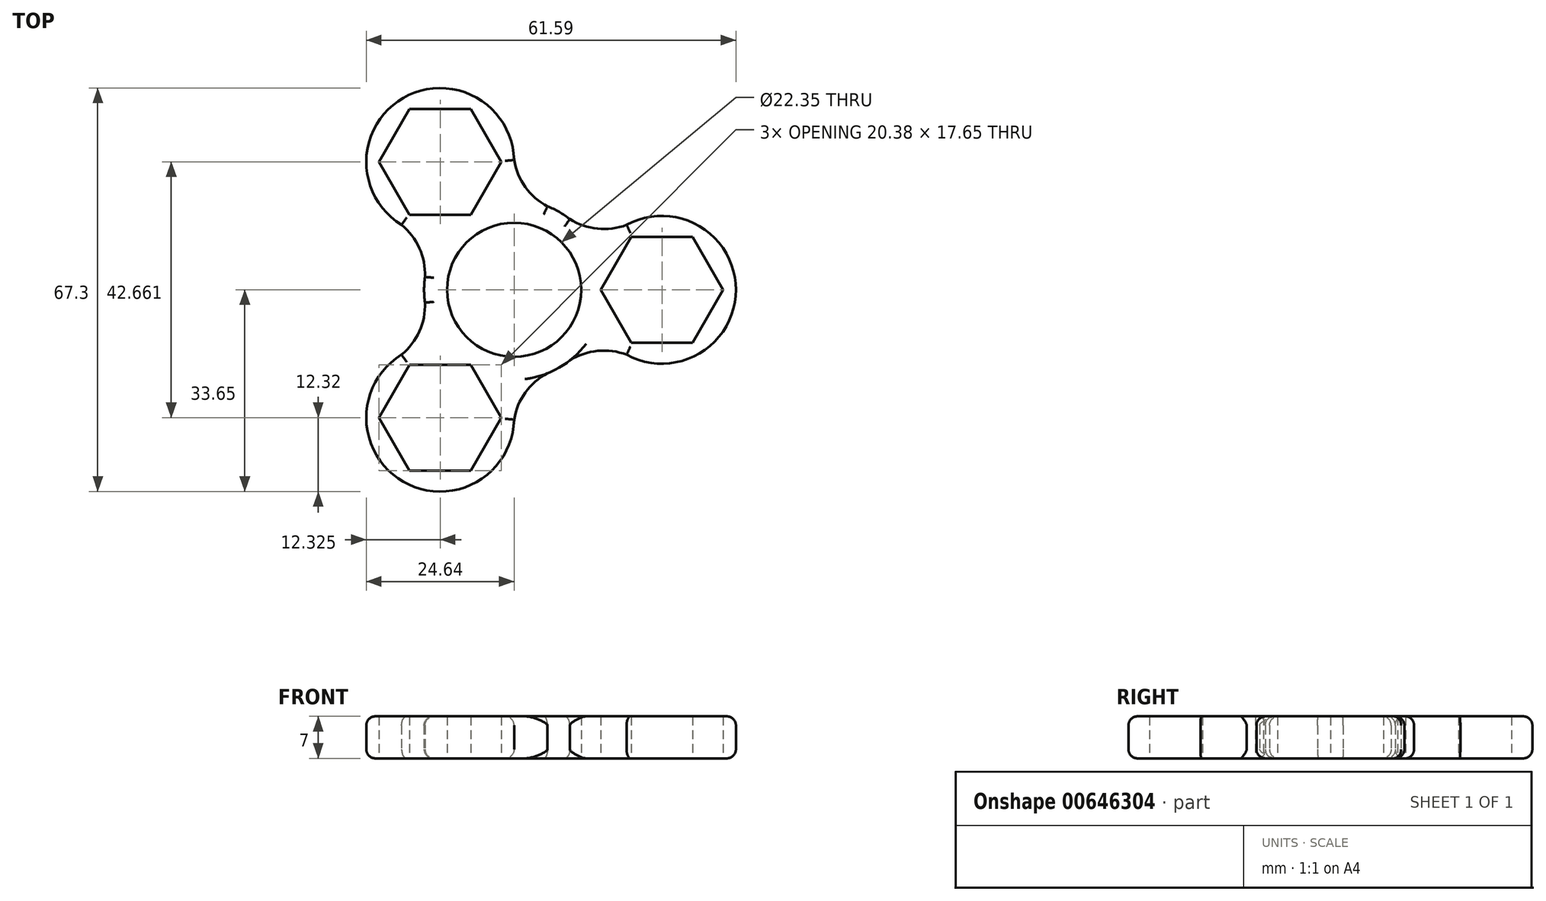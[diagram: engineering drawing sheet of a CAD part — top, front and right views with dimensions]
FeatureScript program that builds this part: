
annotation { "Feature Type Name" : "Feature", "Feature Type Description" : "" }
export const myFeature = defineFeature(function(context is Context, id is Id, definition is map)
    precondition{}
    {
        {
            var Q0;
            Q0=qCreatedBy(makeId("Top.planeOp"),FACE);
            var sketch = newSketch(context, id + "F0", { "sketchPlane" : qUnion([Q0])});
            skCircle(sketch, "E0", {"center": v(0, 0) * mm, "radius": 11.18 * mm});
            skArc(sketch, "E1", {"start": v(9.28, 11.79) * mm, "mid": v(7.5, 13) * mm, "end": v(5.57, 13.93) * mm});
            skLineSegment(sketch, "E2", {"start": v(0, 0) * mm, "end": v(35, 0) * mm, "construction": true});
            skCircle(sketch, "E3.cCircle", {"center": v(24.63, 0) * mm, "radius": 8.82 * mm, "construction": true});
            skLineSegment(sketch, "E3.0", {"start": v(19.54, 8.82) * mm, "end": v(29.73, 8.82) * mm});
            skLineSegment(sketch, "E3.1", {"start": v(29.73, 8.82) * mm, "end": v(34.82, 0) * mm});
            skLineSegment(sketch, "E3.2", {"start": v(34.82, 0) * mm, "end": v(29.73, -8.82) * mm});
            skLineSegment(sketch, "E3.3", {"start": v(29.73, -8.82) * mm, "end": v(19.54, -8.82) * mm});
            skLineSegment(sketch, "E3.4", {"start": v(19.54, -8.82) * mm, "end": v(14.44, 0) * mm});
            skLineSegment(sketch, "E3.5", {"start": v(14.44, 0) * mm, "end": v(19.54, 8.82) * mm});
            skPoint(sketch, "E3.0.midPoint", {"position": v(24.63, 8.82) * mm});
            skArc(sketch, "E4", {"start": v(18.75, -10.83) * mm, "mid": v(36.95, 0) * mm, "end": v(18.75, 10.83) * mm});
            skArc(sketch, "E5", {"start": v(18.75, -10.83) * mm, "mid": v(13.9, -10.2) * mm, "end": v(9.28, -11.79) * mm});
            skArc(sketch, "E6.MirrorCS", {"start": v(18.75, 10.83) * mm, "mid": v(13.9, 10.2) * mm, "end": v(9.28, 11.79) * mm});
            skPoint(sketch, "E7.orphan", {"position": v(13.8, 5.88) * mm});
            skLineSegment(sketch, "E8.1.0", {"start": v(-7.22, 12.5) * mm, "end": v(-17.41, 12.5) * mm});
            skPoint(sketch, "E8.1.1", {"position": v(-19.96, 16.92) * mm});
            skArc(sketch, "E8.1.2", {"start": v(-18.75, 10.82) * mm, "mid": v(-15.78, 6.94) * mm, "end": v(-14.85, 2.14) * mm});
            skArc(sketch, "E8.1.3", {"start": v(0, 21.65) * mm, "mid": v(-18.48, 32) * mm, "end": v(-18.75, 10.82) * mm});
            skLineSegment(sketch, "E8.1.4", {"start": v(0, 0) * mm, "end": v(-17.5, 30.31) * mm, "construction": true});
            skCircle(sketch, "E8.1.5", {"center": v(-12.32, 21.33) * mm, "radius": 8.82 * mm, "construction": true});
            skLineSegment(sketch, "E8.1.6", {"start": v(-17.41, 12.5) * mm, "end": v(-22.5, 21.33) * mm});
            skLineSegment(sketch, "E8.1.7", {"start": v(-22.5, 21.33) * mm, "end": v(-17.41, 30.16) * mm});
            skLineSegment(sketch, "E8.1.8", {"start": v(-17.41, 30.16) * mm, "end": v(-7.22, 30.16) * mm});
            skLineSegment(sketch, "E8.1.9", {"start": v(-7.22, 30.16) * mm, "end": v(-2.12, 21.33) * mm});
            skArc(sketch, "E8.1.10", {"start": v(0, 21.65) * mm, "mid": v(1.88, 17.13) * mm, "end": v(5.57, 13.93) * mm});
            skLineSegment(sketch, "E8.1.11", {"start": v(-2.12, 21.33) * mm, "end": v(-7.22, 12.5) * mm});
            skLineSegment(sketch, "E8.2.0", {"start": v(-7.22, -12.5) * mm, "end": v(-2.12, -21.33) * mm});
            skPoint(sketch, "E8.2.1", {"position": v(-4.67, -25.74) * mm});
            skArc(sketch, "E8.2.2", {"start": v(0, -21.65) * mm, "mid": v(1.88, -17.13) * mm, "end": v(5.57, -13.93) * mm});
            skArc(sketch, "E8.2.3", {"start": v(-18.75, -10.82) * mm, "mid": v(-18.48, -32) * mm, "end": v(0, -21.65) * mm});
            skLineSegment(sketch, "E8.2.4", {"start": v(0, 0) * mm, "end": v(-17.5, -30.31) * mm, "construction": true});
            skCircle(sketch, "E8.2.5", {"center": v(-12.32, -21.33) * mm, "radius": 8.82 * mm, "construction": true});
            skLineSegment(sketch, "E8.2.6", {"start": v(-2.12, -21.33) * mm, "end": v(-7.22, -30.16) * mm});
            skLineSegment(sketch, "E8.2.7", {"start": v(-7.22, -30.16) * mm, "end": v(-17.41, -30.16) * mm});
            skLineSegment(sketch, "E8.2.8", {"start": v(-17.41, -30.16) * mm, "end": v(-22.5, -21.33) * mm});
            skLineSegment(sketch, "E8.2.9", {"start": v(-22.5, -21.33) * mm, "end": v(-17.41, -12.5) * mm});
            skArc(sketch, "E8.2.10", {"start": v(-18.75, -10.82) * mm, "mid": v(-15.78, -6.94) * mm, "end": v(-14.85, -2.14) * mm});
            skLineSegment(sketch, "E8.2.11", {"start": v(-17.41, -12.5) * mm, "end": v(-7.22, -12.5) * mm});
            skPoint(sketch, "E9.trimOffspring.end.orphan", {"position": v(-9.28, 11.79) * mm});
            skArc(sketch, "E10.trimOffspring", {"start": v(-14.85, 2.14) * mm, "mid": v(-15, 0) * mm, "end": v(-14.85, -2.14) * mm});
            skArc(sketch, "E11.trimOffspring", {"start": v(5.57, -13.93) * mm, "mid": v(7.5, -13) * mm, "end": v(9.28, -11.79) * mm});
            skPoint(sketch, "E12.orphan", {"position": v(-9.28, -11.79) * mm});
            skSolve(sketch);
        }
        {
            var Q0;
            Q0=makeQuery(id+"F0.imprint","IMPRINT",FACE,{"disambiguationData":[TD([[makeQuery(id+"F0.imprint","IMPRINT",EDGE,{"derivedFrom":sQuery(id+"F0.wireOp",EDGE,"E0")}),-1.0]])]});
            extrude(context, id + "F1", {"entities" : qUnion([Q0]), "depth" : 7 * mm, "offsetDistance" : 25 * mm});
        }
        {
            var Q0;
            Q0=makeQuery(id+"F1.opExtrude","CAP_EDGE",EDGE,{"disambiguationData":[OSD([sQuery(id+"F0.wireOp",EDGE,"E8.1.10")])],"isStart":false});
            var Q1;
            Q1=makeQuery(id+"F1.opExtrude","CAP_EDGE",EDGE,{"disambiguationData":[OSD([sQuery(id+"F0.wireOp",EDGE,"E8.1.3")])],"isStart":false});
            var Q2;
            Q2=makeQuery(id+"F1.opExtrude","CAP_EDGE",EDGE,{"disambiguationData":[OSD([sQuery(id+"F0.wireOp",EDGE,"E8.1.2")])],"isStart":false});
            var Q3;
            Q3=makeQuery(id+"F1.opExtrude","CAP_EDGE",EDGE,{"disambiguationData":[OSD([sQuery(id+"F0.wireOp",EDGE,"E10.trimOffspring")])],"isStart":false});
            var Q4;
            Q4=makeQuery(id+"F1.opExtrude","CAP_EDGE",EDGE,{"disambiguationData":[OSD([sQuery(id+"F0.wireOp",EDGE,"E8.2.10")])],"isStart":false});
            var Q5;
            Q5=makeQuery(id+"F1.opExtrude","CAP_EDGE",EDGE,{"disambiguationData":[OSD([sQuery(id+"F0.wireOp",EDGE,"E8.2.3")])],"isStart":false});
            var Q6;
            Q6=makeQuery(id+"F1.opExtrude","CAP_EDGE",EDGE,{"disambiguationData":[OSD([sQuery(id+"F0.wireOp",EDGE,"E8.2.2")])],"isStart":false});
            var Q7;
            Q7=makeQuery(id+"F1.opExtrude","CAP_EDGE",EDGE,{"disambiguationData":[OSD([sQuery(id+"F0.wireOp",EDGE,"E11.trimOffspring")])],"isStart":false});
            var Q8;
            Q8=makeQuery(id+"F1.opExtrude","CAP_EDGE",EDGE,{"disambiguationData":[OSD([sQuery(id+"F0.wireOp",EDGE,"E5")])],"isStart":false});
            var Q9;
            Q9=makeQuery(id+"F1.opExtrude","CAP_EDGE",EDGE,{"disambiguationData":[OSD([sQuery(id+"F0.wireOp",EDGE,"E4")])],"isStart":false});
            var Q10;
            Q10=makeQuery(id+"F1.opExtrude","CAP_EDGE",EDGE,{"disambiguationData":[OSD([sQuery(id+"F0.wireOp",EDGE,"E6.MirrorCS")])],"isStart":false});
            var Q11;
            Q11=makeQuery(id+"F1.opExtrude","CAP_EDGE",EDGE,{"disambiguationData":[OSD([sQuery(id+"F0.wireOp",EDGE,"E1")])],"isStart":false});
            fillet(context, id + "F2", {"entities" : qUnion([Q0, Q1, Q2, Q3, Q4, Q5, Q6, Q7, Q8, Q9, Q10, Q11]), "radius" : 1.5 * mm, "tangentPropagation" : true, "allowEdgeOverflow" : false});
        }
        {
            var Q0;
            Q0=makeQuery(id+"F1.opExtrude","CAP_EDGE",EDGE,{"disambiguationData":[OSD([sQuery(id+"F0.wireOp",EDGE,"E8.1.3")])],"isStart":true});
            var Q1;
            Q1=makeQuery(id+"F1.opExtrude","CAP_EDGE",EDGE,{"disambiguationData":[OSD([sQuery(id+"F0.wireOp",EDGE,"E8.1.10")])],"isStart":true});
            var Q2;
            Q2=makeQuery(id+"F1.opExtrude","CAP_EDGE",EDGE,{"disambiguationData":[OSD([sQuery(id+"F0.wireOp",EDGE,"E1")])],"isStart":true});
            var Q3;
            Q3=makeQuery(id+"F1.opExtrude","CAP_EDGE",EDGE,{"disambiguationData":[OSD([sQuery(id+"F0.wireOp",EDGE,"E6.MirrorCS")])],"isStart":true});
            var Q4;
            Q4=makeQuery(id+"F1.opExtrude","CAP_EDGE",EDGE,{"disambiguationData":[OSD([sQuery(id+"F0.wireOp",EDGE,"E4")])],"isStart":true});
            var Q5;
            Q5=makeQuery(id+"F1.opExtrude","CAP_EDGE",EDGE,{"disambiguationData":[OSD([sQuery(id+"F0.wireOp",EDGE,"E5")])],"isStart":true});
            var Q6;
            Q6=makeQuery(id+"F1.opExtrude","CAP_EDGE",EDGE,{"disambiguationData":[OSD([sQuery(id+"F0.wireOp",EDGE,"E11.trimOffspring")])],"isStart":true});
            var Q7;
            Q7=makeQuery(id+"F1.opExtrude","CAP_EDGE",EDGE,{"disambiguationData":[OSD([sQuery(id+"F0.wireOp",EDGE,"E8.2.2")])],"isStart":true});
            var Q8;
            Q8=makeQuery(id+"F1.opExtrude","CAP_EDGE",EDGE,{"disambiguationData":[OSD([sQuery(id+"F0.wireOp",EDGE,"E8.2.3")])],"isStart":true});
            var Q9;
            Q9=makeQuery(id+"F1.opExtrude","CAP_EDGE",EDGE,{"disambiguationData":[OSD([sQuery(id+"F0.wireOp",EDGE,"E8.2.10")])],"isStart":true});
            var Q10;
            Q10=makeQuery(id+"F1.opExtrude","CAP_EDGE",EDGE,{"disambiguationData":[OSD([sQuery(id+"F0.wireOp",EDGE,"E10.trimOffspring")])],"isStart":true});
            var Q11;
            Q11=makeQuery(id+"F1.opExtrude","CAP_EDGE",EDGE,{"disambiguationData":[OSD([sQuery(id+"F0.wireOp",EDGE,"E8.1.2")])],"isStart":true});
            fillet(context, id + "F3", {"entities" : qUnion([Q0, Q1, Q2, Q3, Q4, Q5, Q6, Q7, Q8, Q9, Q10, Q11]), "radius" : 1.5 * mm, "tangentPropagation" : true, "allowEdgeOverflow" : false});
        }
    });
